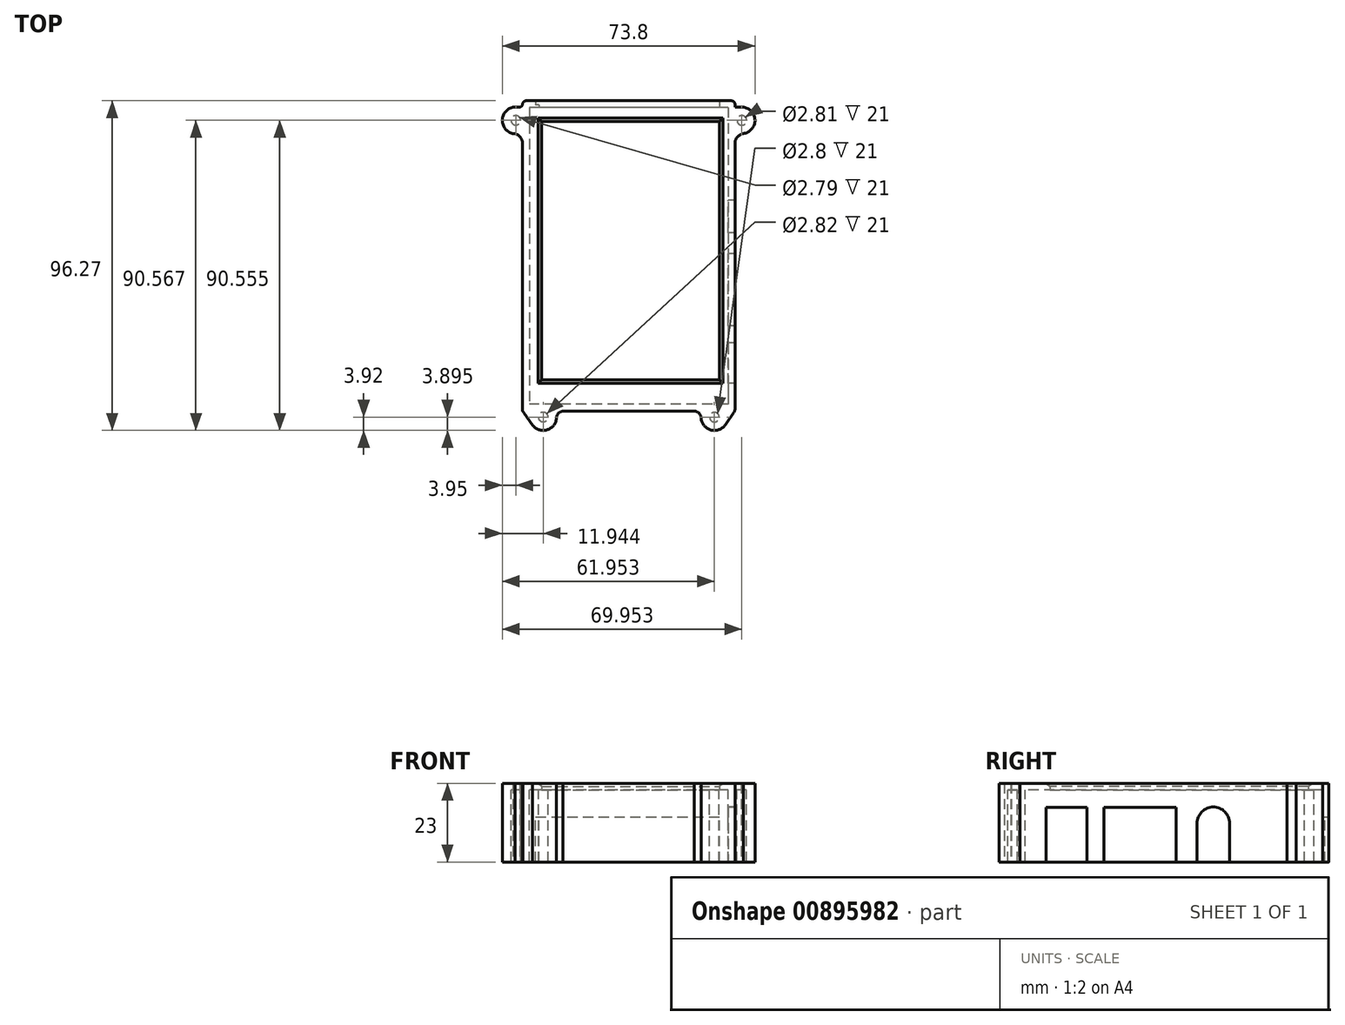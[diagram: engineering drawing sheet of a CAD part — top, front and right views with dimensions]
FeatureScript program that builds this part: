
annotation { "Feature Type Name" : "Feature", "Feature Type Description" : "" }
export const myFeature = defineFeature(function(context is Context, id is Id, definition is map)
    precondition{}
    {
        {
            var Q0;
            Q0=qCreatedBy(makeId("Top.planeOp"),FACE);
            var sketch = newSketch(context, id + "F0", { "sketchPlane" : qUnion([Q0])});
            skLineSegment(sketch, "E0.bottom", {"start": v(21.99, 47.07) * mm, "end": v(-36.05, 47.07) * mm});
            skLineSegment(sketch, "E0.top", {"start": v(21.99, -39.6) * mm, "end": v(-36.05, -39.6) * mm});
            skLineSegment(sketch, "E0.left", {"start": v(21.99, 47.07) * mm, "end": v(21.99, -39.6) * mm});
            skLineSegment(sketch, "E0.right", {"start": v(-36.05, 47.07) * mm, "end": v(-36.05, -39.6) * mm});
            skLineSegment(sketch, "E1.bottom", {"start": v(23.99, 49.03) * mm, "end": v(-38, 49.03) * mm});
            skLineSegment(sketch, "E1.top", {"start": v(23.99, -41.6) * mm, "end": v(-38, -41.6) * mm});
            skLineSegment(sketch, "E1.left", {"start": v(23.99, 49.03) * mm, "end": v(23.99, -41.6) * mm});
            skLineSegment(sketch, "E1.right", {"start": v(-38, 49.03) * mm, "end": v(-38, -41.6) * mm});
            skCircle(sketch, "E2", {"center": v(26, 43.32) * mm, "radius": 1.4 * mm});
            skCircle(sketch, "E3", {"center": v(18, -43.34) * mm, "radius": 1.4 * mm});
            skCircle(sketch, "E4", {"center": v(-32, -43.32) * mm, "radius": 1.41 * mm});
            skCircle(sketch, "E5", {"center": v(-40, 43.33) * mm, "radius": 1.4 * mm});
            skLineSegment(sketch, "E6.bottom", {"start": v(2.04, 49.03) * mm, "end": v(-16.27, 49.03) * mm});
            skLineSegment(sketch, "E6.top", {"start": v(2.04, 47.8) * mm, "end": v(-16.27, 47.8) * mm});
            skLineSegment(sketch, "E6.left", {"start": v(2.04, 49.03) * mm, "end": v(2.04, 47.8) * mm});
            skLineSegment(sketch, "E6.right", {"start": v(-16.27, 49.03) * mm, "end": v(-16.27, 47.8) * mm});
            skLineSegment(sketch, "E7.bottom", {"start": v(-17.75, 49.03) * mm, "end": v(-34.26, 49.03) * mm});
            skLineSegment(sketch, "E7.top", {"start": v(-17.75, 47.8) * mm, "end": v(-34.26, 47.8) * mm});
            skLineSegment(sketch, "E7.left", {"start": v(-17.75, 49.03) * mm, "end": v(-17.75, 47.8) * mm});
            skLineSegment(sketch, "E7.right", {"start": v(-34.26, 49.03) * mm, "end": v(-34.26, 47.8) * mm});
            skLineSegment(sketch, "E8", {"start": v(-33.26, 47.8) * mm, "end": v(-33.26, 47) * mm});
            skLineSegment(sketch, "E9", {"start": v(-15.27, 47.8) * mm, "end": v(-15.27, 45.98) * mm});
            skLineSegment(sketch, "E10", {"start": v(-15.27, 45.98) * mm, "end": v(-18.7, 45.98) * mm});
            skLineSegment(sketch, "E11", {"start": v(-18.7, 45.98) * mm, "end": v(-18.7, 47.8) * mm});
            skLineSegment(sketch, "E12", {"start": v(2.04, 47.8) * mm, "end": v(-0.71, 47.8) * mm});
            skLineSegment(sketch, "E13", {"start": v(-0.71, 47.8) * mm, "end": v(-0.71, 45.98) * mm});
            skLineSegment(sketch, "E14", {"start": v(-0.71, 45.98) * mm, "end": v(2.04, 45.98) * mm});
            skLineSegment(sketch, "E15", {"start": v(2.04, 45.98) * mm, "end": v(2.04, 47.07) * mm});
            skLineSegment(sketch, "E16", {"start": v(2.04, 47.07) * mm, "end": v(2.04, 49.03) * mm});
            skLineSegment(sketch, "E17", {"start": v(2.04, 49.03) * mm, "end": v(2.04, 49.03) * mm});
            skLineSegment(sketch, "E18", {"start": v(19.42, 49.03) * mm, "end": v(19.42, 47.07) * mm});
            skArc(sketch, "E19", {"start": v(26.4, 39.47) * mm, "mid": v(29.84, 43.42) * mm, "end": v(26.2, 47.18) * mm});
            skArc(sketch, "E20", {"start": v(26.2, 47.18) * mm, "mid": v(26, 47.19) * mm, "end": v(25.8, 47.18) * mm});
            skLineSegment(sketch, "E21", {"start": v(25.8, 47.18) * mm, "end": v(23.99, 47.18) * mm});
            skArc(sketch, "E22", {"start": v(26.4, 39.47) * mm, "mid": v(24.75, 38.5) * mm, "end": v(23.99, 36.76) * mm});
            skLineSegment(sketch, "E23.bottom", {"start": v(23.99, 21.28) * mm, "end": v(22.99, 21.28) * mm});
            skLineSegment(sketch, "E23.top", {"start": v(23.99, 11.78) * mm, "end": v(22.99, 11.78) * mm});
            skLineSegment(sketch, "E23.left", {"start": v(23.99, 21.28) * mm, "end": v(23.99, 11.78) * mm});
            skLineSegment(sketch, "E23.right", {"start": v(22.99, 21.28) * mm, "end": v(22.99, 11.78) * mm});
            skLineSegment(sketch, "E24.bottom", {"start": v(22.99, 13) * mm, "end": v(21.99, 13) * mm});
            skLineSegment(sketch, "E24.top", {"start": v(22.99, 20.04) * mm, "end": v(21.99, 20.04) * mm});
            skLineSegment(sketch, "E24.left", {"start": v(22.99, 13) * mm, "end": v(22.99, 20.04) * mm});
            skLineSegment(sketch, "E24.right", {"start": v(21.99, 13) * mm, "end": v(21.99, 20.04) * mm});
            skLineSegment(sketch, "E25", {"start": v(23.99, 5.53) * mm, "end": v(22.99, 5.53) * mm});
            skLineSegment(sketch, "E26", {"start": v(22.99, 5.53) * mm, "end": v(22.5, 5.04) * mm});
            skLineSegment(sketch, "E27", {"start": v(22.5, 5.04) * mm, "end": v(22.5, -15.01) * mm});
            skLineSegment(sketch, "E28", {"start": v(22.5, -15.01) * mm, "end": v(22.99, -15.47) * mm});
            skLineSegment(sketch, "E29", {"start": v(22.99, -15.47) * mm, "end": v(23.99, -15.47) * mm});
            skLineSegment(sketch, "E30", {"start": v(22.99, 5.53) * mm, "end": v(22.99, -15.47) * mm});
            skLineSegment(sketch, "E31", {"start": v(21.99, 7) * mm, "end": v(21.5, 6.56) * mm});
            skLineSegment(sketch, "E32", {"start": v(21.5, 6.56) * mm, "end": v(21.5, 3.27) * mm});
            skLineSegment(sketch, "E33", {"start": v(21.5, 3.27) * mm, "end": v(22.5, 3.27) * mm});
            skLineSegment(sketch, "E34", {"start": v(21.5, 3.27) * mm, "end": v(21.5, -13.23) * mm});
            skLineSegment(sketch, "E35", {"start": v(21.5, -13.23) * mm, "end": v(22.5, -13.23) * mm});
            skLineSegment(sketch, "E36", {"start": v(21.5, -13.23) * mm, "end": v(21.5, -16.5) * mm});
            skLineSegment(sketch, "E37", {"start": v(21.5, -16.5) * mm, "end": v(21.99, -16.96) * mm});
            skLineSegment(sketch, "E38", {"start": v(21.99, -16.96) * mm, "end": v(21.99, -18.86) * mm});
            skLineSegment(sketch, "E39", {"start": v(21.99, -18.86) * mm, "end": v(21.5, -19.34) * mm});
            skLineSegment(sketch, "E40", {"start": v(21.5, -19.34) * mm, "end": v(21.5, -33.42) * mm});
            skLineSegment(sketch, "E41", {"start": v(21.5, -33.42) * mm, "end": v(22.62, -34.44) * mm});
            skLineSegment(sketch, "E42", {"start": v(21.5, -21.89) * mm, "end": v(22.5, -21.85) * mm});
            skLineSegment(sketch, "E43", {"start": v(21.5, -30.87) * mm, "end": v(22.5, -30.87) * mm});
            skLineSegment(sketch, "E44", {"start": v(23.99, -20.4) * mm, "end": v(23.01, -20.4) * mm});
            skLineSegment(sketch, "E45", {"start": v(23.01, -20.4) * mm, "end": v(23.01, -32.4) * mm});
            skLineSegment(sketch, "E46", {"start": v(23.01, -32.4) * mm, "end": v(23.99, -32.4) * mm});
            skLineSegment(sketch, "E47", {"start": v(23.01, -20.4) * mm, "end": v(22.5, -20.86) * mm});
            skLineSegment(sketch, "E48", {"start": v(22.5, -20.86) * mm, "end": v(22.5, -31.86) * mm});
            skLineSegment(sketch, "E49", {"start": v(22.5, -31.86) * mm, "end": v(23.01, -32.4) * mm});
            skLineSegment(sketch, "E50", {"start": v(9.84, -39.6) * mm, "end": v(-0.16, -39.6) * mm});
            skLineSegment(sketch, "E51", {"start": v(-0.16, -39.6) * mm, "end": v(-0.16, -40.6) * mm});
            skLineSegment(sketch, "E52", {"start": v(-0.16, -40.6) * mm, "end": v(1.35, -40.6) * mm});
            skLineSegment(sketch, "E53", {"start": v(1.35, -40.6) * mm, "end": v(1.35, -41.6) * mm});
            skLineSegment(sketch, "E54", {"start": v(9.84, -39.6) * mm, "end": v(9.84, -41.6) * mm});
            skLineSegment(sketch, "E55", {"start": v(-23.65, -39.6) * mm, "end": v(-23.65, -41.6) * mm});
            skLineSegment(sketch, "E56", {"start": v(-13.67, -39.6) * mm, "end": v(-13.67, -40.58) * mm});
            skLineSegment(sketch, "E57", {"start": v(-13.67, -40.58) * mm, "end": v(-15.15, -40.58) * mm});
            skLineSegment(sketch, "E58", {"start": v(-15.15, -40.58) * mm, "end": v(-15.15, -41.6) * mm});
            skLineSegment(sketch, "E59", {"start": v(-0.66, -39.1) * mm, "end": v(-13.16, -39.1) * mm});
            skArc(sketch, "E60", {"start": v(-0.16, -39.6) * mm, "mid": v(-0.3, -39.24) * mm, "end": v(-0.66, -39.1) * mm});
            skArc(sketch, "E61", {"start": v(-13.16, -39.1) * mm, "mid": v(-13.51, -39.24) * mm, "end": v(-13.66, -39.6) * mm});
            skArc(sketch, "E62", {"start": v(-35.1, -45.7) * mm, "mid": v(-30.94, -47.08) * mm, "end": v(-28.12, -43.72) * mm});
            skArc(sketch, "E63", {"start": v(-26.26, -41.6) * mm, "mid": v(-27.63, -42.28) * mm, "end": v(-28.12, -43.72) * mm});
            skLineSegment(sketch, "E64", {"start": v(-35.1, -45.7) * mm, "end": v(-37.6, -42.18) * mm});
            skArc(sketch, "E65", {"start": v(-40.81, 47.19) * mm, "mid": v(-43.93, 43.02) * mm, "end": v(-40.2, 39.39) * mm});
            skArc(sketch, "E66", {"start": v(-38, 36.69) * mm, "mid": v(-38.68, 38.39) * mm, "end": v(-40.2, 39.39) * mm});
            skArc(sketch, "E67", {"start": v(-38.87, 47.19) * mm, "mid": v(-38.28, 47.5) * mm, "end": v(-38, 48.1) * mm});
            skLineSegment(sketch, "E68", {"start": v(-38.87, 47.19) * mm, "end": v(-40.81, 47.19) * mm});
            skArc(sketch, "E69", {"start": v(14.14, -43.87) * mm, "mid": v(17.09, -47.13) * mm, "end": v(21.2, -45.57) * mm});
            skArc(sketch, "E70", {"start": v(23.68, -42.01) * mm, "mid": v(23.89, -41.6) * mm, "end": v(23.99, -41.15) * mm});
            skLineSegment(sketch, "E71", {"start": v(23.68, -42.01) * mm, "end": v(21.2, -45.57) * mm});
            skArc(sketch, "E72", {"start": v(14.09, -43.4) * mm, "mid": v(13.46, -42.14) * mm, "end": v(12.16, -41.6) * mm});
            skLineSegment(sketch, "E73", {"start": v(14.09, -43.4) * mm, "end": v(14.14, -43.87) * mm});
            skPoint(sketch, "E74", {"position": v(-37.9, -41.6) * mm});
            skArc(sketch, "E75", {"start": v(-37.9, -41.6) * mm, "mid": v(-37.77, -41.9) * mm, "end": v(-37.6, -42.18) * mm});
            skArc(sketch, "E76", {"start": v(-38, -41.1) * mm, "mid": v(-37.98, -41.36) * mm, "end": v(-37.9, -41.6) * mm});
            skLineSegment(sketch, "E77", {"start": v(21.55, 21.53) * mm, "end": v(23.99, 21.53) * mm, "construction": true});
            skLineSegment(sketch, "E78.bottom", {"start": v(-32.5, -32.47) * mm, "end": v(19.5, -32.47) * mm});
            skLineSegment(sketch, "E78.top", {"start": v(-32.5, 43.03) * mm, "end": v(19.5, 43.03) * mm});
            skLineSegment(sketch, "E78.left", {"start": v(-32.5, -32.47) * mm, "end": v(-32.5, 43.03) * mm});
            skLineSegment(sketch, "E78.right", {"start": v(19.5, -32.47) * mm, "end": v(19.5, 43.03) * mm});
            skSolve(sketch);
        }
        {
            var Q0;
            {var subQ3=sQuery(id+"F0.wireOp",EDGE,"E6.left");Q0=makeQuery(id+"F0.imprint","IMPRINT",FACE,{"disambiguationData":[TD([[makeQuery(id+"F0.imprint","IMPRINT",EDGE,{"derivedFrom":subQ3}),1.0]])]});}
            var Q1;
            {var subQ0=sQuery(id+"F0.wireOp",EDGE,"E18");Q1=makeQuery(id+"F0.imprint","IMPRINT",FACE,{"disambiguationData":[TD([[makeQuery(id+"F0.imprint","IMPRINT",EDGE,{"derivedFrom":subQ0}),1.0]])]});}
            var Q2;
            Q2=makeQuery(id+"F0.imprint","IMPRINT",FACE,{"disambiguationData":[TD([[makeQuery(id+"F0.imprint","IMPRINT",EDGE,{"derivedFrom":sQuery(id+"F0.wireOp",EDGE,"E2")}),-1.0]])]});
            var Q3;
            {var subQ0=sQuery(id+"F0.wireOp",EDGE,"E24.bottom");Q3=makeQuery(id+"F0.imprint","IMPRINT",FACE,{"disambiguationData":[TD([[makeQuery(id+"F0.imprint","IMPRINT",EDGE,{"derivedFrom":subQ0}),-1.0]])]});}
            var Q4;
            {var subQ3=sQuery(id+"F0.wireOp",EDGE,"E23.bottom");Q4=makeQuery(id+"F0.imprint","IMPRINT",FACE,{"disambiguationData":[TD([[makeQuery(id+"F0.imprint","IMPRINT",EDGE,{"derivedFrom":subQ3}),1.0]])]});}
            var Q5;
            {var subQ2=sQuery(id+"F0.wireOp",EDGE,"E23.top");Q5=makeQuery(id+"F0.imprint","IMPRINT",FACE,{"disambiguationData":[TD([[makeQuery(id+"F0.imprint","IMPRINT",EDGE,{"derivedFrom":subQ2}),1.0]])]});}
            var Q6;
            {var subQ0=sQuery(id+"F0.wireOp",EDGE,"E33");var subQ1=sQuery(id+"F0.wireOp",EDGE,"E0.left");var subQ2=makeQuery(id+"F0.imprint","INTERSECT",VERTEX,{"derivedFrom":[subQ1,subQ0]});Q6=makeQuery(id+"F0.imprint","IMPRINT",FACE,{"disambiguationData":[TD([[makeQuery(id+"F0.imprint","IMPRINT",EDGE,{"disambiguationData":[TD([[subQ2,-1.0]])],"derivedFrom":subQ1}),1.0]])]});}
            var Q7;
            {var subQ0=sQuery(id+"F0.wireOp",EDGE,"E25");Q7=makeQuery(id+"F0.imprint","IMPRINT",FACE,{"disambiguationData":[TD([[makeQuery(id+"F0.imprint","IMPRINT",EDGE,{"derivedFrom":subQ0}),1.0]])]});}
            var Q8;
            {var subQ1=sQuery(id+"F0.wireOp",EDGE,"E26");Q8=makeQuery(id+"F0.imprint","IMPRINT",FACE,{"disambiguationData":[TD([[makeQuery(id+"F0.imprint","IMPRINT",EDGE,{"derivedFrom":subQ1}),1.0]])]});}
            var Q9;
            {var subQ21=sQuery(id+"F0.wireOp",EDGE,"E0.right");Q9=makeQuery(id+"F0.imprint","IMPRINT",FACE,{"disambiguationData":[TD([[makeQuery(id+"F0.imprint","IMPRINT",EDGE,{"derivedFrom":subQ21}),1.0]])]});}
            var Q10;
            {var subQ1=sQuery(id+"F0.wireOp",EDGE,"E28");Q10=makeQuery(id+"F0.imprint","IMPRINT",FACE,{"disambiguationData":[TD([[makeQuery(id+"F0.imprint","IMPRINT",EDGE,{"derivedFrom":subQ1}),-1.0]])]});}
            var Q11;
            {var subQ4=sQuery(id+"F0.wireOp",EDGE,"E36");Q11=makeQuery(id+"F0.imprint","IMPRINT",FACE,{"disambiguationData":[TD([[makeQuery(id+"F0.imprint","IMPRINT",EDGE,{"derivedFrom":subQ4}),1.0]])]});}
            var Q12;
            {var subQ0=sQuery(id+"F0.wireOp",EDGE,"E39");Q12=makeQuery(id+"F0.imprint","IMPRINT",FACE,{"disambiguationData":[TD([[makeQuery(id+"F0.imprint","IMPRINT",EDGE,{"derivedFrom":subQ0}),1.0]])]});}
            var Q13;
            {var subQ0=sQuery(id+"F0.wireOp",EDGE,"E42");var subQ1=sQuery(id+"F0.wireOp",EDGE,"E0.left");var subQ2=makeQuery(id+"F0.imprint","INTERSECT",VERTEX,{"derivedFrom":[subQ1,subQ0]});Q13=makeQuery(id+"F0.imprint","IMPRINT",FACE,{"disambiguationData":[TD([[makeQuery(id+"F0.imprint","IMPRINT",EDGE,{"disambiguationData":[TD([[subQ2,-1.0]])],"derivedFrom":subQ1}),-1.0]])]});}
            var Q14;
            {var subQ0=sQuery(id+"F0.wireOp",EDGE,"E42");var subQ1=sQuery(id+"F0.wireOp",EDGE,"E0.left");var subQ2=makeQuery(id+"F0.imprint","INTERSECT",VERTEX,{"derivedFrom":[subQ1,subQ0]});Q14=makeQuery(id+"F0.imprint","IMPRINT",FACE,{"disambiguationData":[TD([[makeQuery(id+"F0.imprint","IMPRINT",EDGE,{"disambiguationData":[TD([[subQ2,-1.0]])],"derivedFrom":subQ1}),1.0]])]});}
            var Q15;
            Q15=makeQuery(id+"F0.imprint","IMPRINT",FACE,{"disambiguationData":[TD([[makeQuery(id+"F0.imprint","IMPRINT",EDGE,{"derivedFrom":sQuery(id+"F0.wireOp",EDGE,"E45")}),-1.0]])]});
            var Q16;
            {var subQ0=sQuery(id+"F0.wireOp",EDGE,"E44");Q16=makeQuery(id+"F0.imprint","IMPRINT",FACE,{"disambiguationData":[TD([[makeQuery(id+"F0.imprint","IMPRINT",EDGE,{"derivedFrom":subQ0}),1.0]])]});}
            var Q17;
            {var subQ5=sQuery(id+"F0.wireOp",EDGE,"E34");Q17=makeQuery(id+"F0.imprint","IMPRINT",FACE,{"disambiguationData":[TD([[makeQuery(id+"F0.imprint","IMPRINT",EDGE,{"derivedFrom":subQ5}),1.0]])]});}
            var Q18;
            {var subQ0=sQuery(id+"F0.wireOp",EDGE,"E31");Q18=makeQuery(id+"F0.imprint","IMPRINT",FACE,{"disambiguationData":[TD([[makeQuery(id+"F0.imprint","IMPRINT",EDGE,{"derivedFrom":subQ0}),1.0]])]});}
            var Q19;
            {var subQ0=sQuery(id+"F0.wireOp",EDGE,"E41");var subQ1=sQuery(id+"F0.wireOp",EDGE,"E0.left");var subQ2=makeQuery(id+"F0.imprint","INTERSECT",VERTEX,{"derivedFrom":[subQ1,subQ0]});Q19=makeQuery(id+"F0.imprint","IMPRINT",FACE,{"disambiguationData":[TD([[makeQuery(id+"F0.imprint","IMPRINT",EDGE,{"disambiguationData":[TD([[subQ2,1.0]])],"derivedFrom":subQ1}),-1.0]])]});}
            var Q20;
            {var subQ1=sQuery(id+"F0.wireOp",EDGE,"E46");Q20=makeQuery(id+"F0.imprint","IMPRINT",FACE,{"disambiguationData":[TD([[makeQuery(id+"F0.imprint","IMPRINT",EDGE,{"derivedFrom":subQ1}),-1.0]])]});}
            var Q21;
            Q21=makeQuery(id+"F0.imprint","IMPRINT",FACE,{"disambiguationData":[TD([[makeQuery(id+"F0.imprint","IMPRINT",EDGE,{"derivedFrom":sQuery(id+"F0.wireOp",EDGE,"E3")}),-1.0]])]});
            var Q22;
            {var subQ1=sQuery(id+"F0.wireOp",EDGE,"E55");Q22=makeQuery(id+"F0.imprint","IMPRINT",FACE,{"disambiguationData":[TD([[makeQuery(id+"F0.imprint","IMPRINT",EDGE,{"derivedFrom":subQ1}),1.0]])]});}
            var Q23;
            {var subQ4=sQuery(id+"F0.wireOp",EDGE,"E0.right");Q23=makeQuery(id+"F0.imprint","IMPRINT",FACE,{"disambiguationData":[TD([[makeQuery(id+"F0.imprint","IMPRINT",EDGE,{"derivedFrom":subQ4}),-1.0]])]});}
            var Q24;
            {var subQ0=sQuery(id+"F0.wireOp",EDGE,"E51");Q24=makeQuery(id+"F0.imprint","IMPRINT",FACE,{"disambiguationData":[TD([[makeQuery(id+"F0.imprint","IMPRINT",EDGE,{"derivedFrom":subQ0}),-1.0]])]});}
            var Q25;
            {var subQ0=sQuery(id+"F0.wireOp",EDGE,"E51");Q25=makeQuery(id+"F0.imprint","IMPRINT",FACE,{"disambiguationData":[TD([[makeQuery(id+"F0.imprint","IMPRINT",EDGE,{"derivedFrom":subQ0}),1.0]])]});}
            var Q26;
            Q26=makeQuery(id+"F0.imprint","IMPRINT",FACE,{"disambiguationData":[TD([[makeQuery(id+"F0.imprint","IMPRINT",EDGE,{"derivedFrom":sQuery(id+"F0.wireOp",EDGE,"E59")}),1.0]])]});
            var Q27;
            Q27=makeQuery(id+"F0.imprint","IMPRINT",FACE,{"disambiguationData":[TD([[makeQuery(id+"F0.imprint","IMPRINT",EDGE,{"derivedFrom":sQuery(id+"F0.wireOp",EDGE,"E4")}),-1.0]])]});
            var Q28;
            Q28=makeQuery(id+"F0.imprint","IMPRINT",FACE,{"disambiguationData":[TD([[makeQuery(id+"F0.imprint","IMPRINT",EDGE,{"derivedFrom":sQuery(id+"F0.wireOp",EDGE,"E5")}),-1.0]])]});
            var Q29;
            {var subQ0=sQuery(id+"F0.wireOp",EDGE,"E8");var subQ1=sQuery(id+"F0.wireOp",EDGE,"E0.bottom");var subQ2=makeQuery(id+"F0.imprint","INTERSECT",VERTEX,{"derivedFrom":[subQ1,subQ0]});Q29=makeQuery(id+"F0.imprint","IMPRINT",FACE,{"disambiguationData":[TD([[makeQuery(id+"F0.imprint","IMPRINT",EDGE,{"disambiguationData":[TD([[subQ2,1.0]])],"derivedFrom":subQ1}),-1.0]])]});}
            var Q30;
            {var subQ2=sQuery(id+"F0.wireOp",EDGE,"E7.left");Q30=makeQuery(id+"F0.imprint","IMPRINT",FACE,{"disambiguationData":[TD([[makeQuery(id+"F0.imprint","IMPRINT",EDGE,{"derivedFrom":subQ2}),-1.0]])]});}
            var Q31;
            {var subQ5=sQuery(id+"F0.wireOp",EDGE,"E10");Q31=makeQuery(id+"F0.imprint","IMPRINT",FACE,{"disambiguationData":[TD([[makeQuery(id+"F0.imprint","IMPRINT",EDGE,{"derivedFrom":subQ5}),-1.0]])]});}
            var Q32;
            {var subQ0=sQuery(id+"F0.wireOp",EDGE,"E6.right");Q32=makeQuery(id+"F0.imprint","IMPRINT",FACE,{"disambiguationData":[TD([[makeQuery(id+"F0.imprint","IMPRINT",EDGE,{"derivedFrom":subQ0}),-1.0]])]});}
            var Q33;
            {var subQ0=sQuery(id+"F0.wireOp",EDGE,"E9");var subQ1=sQuery(id+"F0.wireOp",EDGE,"E0.bottom");var subQ2=makeQuery(id+"F0.imprint","INTERSECT",VERTEX,{"derivedFrom":[subQ1,subQ0]});Q33=makeQuery(id+"F0.imprint","IMPRINT",FACE,{"disambiguationData":[TD([[makeQuery(id+"F0.imprint","IMPRINT",EDGE,{"disambiguationData":[TD([[subQ2,1.0]])],"derivedFrom":subQ1}),-1.0]])]});}
            var Q34;
            {var subQ4=sQuery(id+"F0.wireOp",EDGE,"E6.left");Q34=makeQuery(id+"F0.imprint","IMPRINT",FACE,{"disambiguationData":[TD([[makeQuery(id+"F0.imprint","IMPRINT",EDGE,{"derivedFrom":subQ4}),-1.0]])]});}
            var Q35;
            {var subQ4=sQuery(id+"F0.wireOp",EDGE,"E14");Q35=makeQuery(id+"F0.imprint","IMPRINT",FACE,{"disambiguationData":[TD([[makeQuery(id+"F0.imprint","IMPRINT",EDGE,{"derivedFrom":subQ4}),1.0]])]});}
            var Q36;
            {var subQ3=sQuery(id+"F0.wireOp",EDGE,"E16");Q36=makeQuery(id+"F0.imprint","IMPRINT",FACE,{"disambiguationData":[TD([[makeQuery(id+"F0.imprint","IMPRINT",EDGE,{"derivedFrom":subQ3}),1.0]])]});}
            var Q37;
            Q37=makeQuery(id+"F0.imprint","IMPRINT",FACE,{"disambiguationData":[TD([[makeQuery(id+"F0.imprint","IMPRINT",EDGE,{"derivedFrom":sQuery(id+"F0.wireOp",EDGE,"E4")}),1.0]])]});
            var Q38;
            Q38=makeQuery(id+"F0.imprint","IMPRINT",FACE,{"disambiguationData":[TD([[makeQuery(id+"F0.imprint","IMPRINT",EDGE,{"derivedFrom":sQuery(id+"F0.wireOp",EDGE,"E5")}),1.0]])]});
            var Q39;
            Q39=makeQuery(id+"F0.imprint","IMPRINT",FACE,{"disambiguationData":[TD([[makeQuery(id+"F0.imprint","IMPRINT",EDGE,{"derivedFrom":sQuery(id+"F0.wireOp",EDGE,"E2")}),1.0]])]});
            var Q40;
            Q40=makeQuery(id+"F0.imprint","IMPRINT",FACE,{"disambiguationData":[TD([[makeQuery(id+"F0.imprint","IMPRINT",EDGE,{"derivedFrom":sQuery(id+"F0.wireOp",EDGE,"E3")}),1.0]])]});
            extrude(context, id + "F1", {"entities" : qUnion([Q0, Q1, Q2, Q3, Q4, Q5, Q6, Q7, Q8, Q9, Q10, Q11, Q12, Q13, Q14, Q15, Q16, Q17, Q18, Q19, Q20, Q21, Q22, Q23, Q24, Q25, Q26, Q27, Q28, Q29, Q30, Q31, Q32, Q33, Q34, Q35, Q36, Q37, Q38, Q39, Q40]), "depth" : 2 * mm, "offsetDistance" : 25 * mm});
        }
        {
            var Q0;
            {var subQ4=sQuery(id+"F0.wireOp",EDGE,"E0.right");Q0=makeQuery(id+"F0.imprint","IMPRINT",FACE,{"disambiguationData":[TD([[makeQuery(id+"F0.imprint","IMPRINT",EDGE,{"derivedFrom":subQ4}),-1.0]])]});}
            var Q1;
            {var subQ1=sQuery(id+"F0.wireOp",EDGE,"E55");Q1=makeQuery(id+"F0.imprint","IMPRINT",FACE,{"disambiguationData":[TD([[makeQuery(id+"F0.imprint","IMPRINT",EDGE,{"derivedFrom":subQ1}),1.0]])]});}
            var Q2;
            Q2=makeQuery(id+"F0.imprint","IMPRINT",FACE,{"disambiguationData":[TD([[makeQuery(id+"F0.imprint","IMPRINT",EDGE,{"derivedFrom":sQuery(id+"F0.wireOp",EDGE,"E4")}),-1.0]])]});
            var Q3;
            Q3=makeQuery(id+"F0.imprint","IMPRINT",FACE,{"disambiguationData":[TD([[makeQuery(id+"F0.imprint","IMPRINT",EDGE,{"derivedFrom":sQuery(id+"F0.wireOp",EDGE,"E3")}),-1.0]])]});
            var Q4;
            {var subQ1=sQuery(id+"F0.wireOp",EDGE,"E46");Q4=makeQuery(id+"F0.imprint","IMPRINT",FACE,{"disambiguationData":[TD([[makeQuery(id+"F0.imprint","IMPRINT",EDGE,{"derivedFrom":subQ1}),-1.0]])]});}
            var Q5;
            {var subQ0=sQuery(id+"F0.wireOp",EDGE,"E51");Q5=makeQuery(id+"F0.imprint","IMPRINT",FACE,{"disambiguationData":[TD([[makeQuery(id+"F0.imprint","IMPRINT",EDGE,{"derivedFrom":subQ0}),1.0]])]});}
            var Q6;
            {var subQ0=sQuery(id+"F0.wireOp",EDGE,"E51");Q6=makeQuery(id+"F0.imprint","IMPRINT",FACE,{"disambiguationData":[TD([[makeQuery(id+"F0.imprint","IMPRINT",EDGE,{"derivedFrom":subQ0}),-1.0]])]});}
            var Q7;
            {var subQ0=sQuery(id+"F0.wireOp",EDGE,"E44");Q7=makeQuery(id+"F0.imprint","IMPRINT",FACE,{"disambiguationData":[TD([[makeQuery(id+"F0.imprint","IMPRINT",EDGE,{"derivedFrom":subQ0}),1.0]])]});}
            var Q8;
            {var subQ1=sQuery(id+"F0.wireOp",EDGE,"E28");Q8=makeQuery(id+"F0.imprint","IMPRINT",FACE,{"disambiguationData":[TD([[makeQuery(id+"F0.imprint","IMPRINT",EDGE,{"derivedFrom":subQ1}),-1.0]])]});}
            var Q9;
            {var subQ0=sQuery(id+"F0.wireOp",EDGE,"E25");Q9=makeQuery(id+"F0.imprint","IMPRINT",FACE,{"disambiguationData":[TD([[makeQuery(id+"F0.imprint","IMPRINT",EDGE,{"derivedFrom":subQ0}),1.0]])]});}
            var Q10;
            {var subQ2=sQuery(id+"F0.wireOp",EDGE,"E23.top");Q10=makeQuery(id+"F0.imprint","IMPRINT",FACE,{"disambiguationData":[TD([[makeQuery(id+"F0.imprint","IMPRINT",EDGE,{"derivedFrom":subQ2}),1.0]])]});}
            var Q11;
            {var subQ3=sQuery(id+"F0.wireOp",EDGE,"E23.bottom");Q11=makeQuery(id+"F0.imprint","IMPRINT",FACE,{"disambiguationData":[TD([[makeQuery(id+"F0.imprint","IMPRINT",EDGE,{"derivedFrom":subQ3}),1.0]])]});}
            var Q12;
            {var subQ0=sQuery(id+"F0.wireOp",EDGE,"E24.bottom");Q12=makeQuery(id+"F0.imprint","IMPRINT",FACE,{"disambiguationData":[TD([[makeQuery(id+"F0.imprint","IMPRINT",EDGE,{"derivedFrom":subQ0}),-1.0]])]});}
            var Q13;
            {var subQ0=sQuery(id+"F0.wireOp",EDGE,"E18");Q13=makeQuery(id+"F0.imprint","IMPRINT",FACE,{"disambiguationData":[TD([[makeQuery(id+"F0.imprint","IMPRINT",EDGE,{"derivedFrom":subQ0}),1.0]])]});}
            var Q14;
            Q14=makeQuery(id+"F0.imprint","IMPRINT",FACE,{"disambiguationData":[TD([[makeQuery(id+"F0.imprint","IMPRINT",EDGE,{"derivedFrom":sQuery(id+"F0.wireOp",EDGE,"E2")}),-1.0]])]});
            var Q15;
            {var subQ3=sQuery(id+"F0.wireOp",EDGE,"E6.left");Q15=makeQuery(id+"F0.imprint","IMPRINT",FACE,{"disambiguationData":[TD([[makeQuery(id+"F0.imprint","IMPRINT",EDGE,{"derivedFrom":subQ3}),1.0]])]});}
            var Q16;
            {var subQ4=sQuery(id+"F0.wireOp",EDGE,"E6.left");Q16=makeQuery(id+"F0.imprint","IMPRINT",FACE,{"disambiguationData":[TD([[makeQuery(id+"F0.imprint","IMPRINT",EDGE,{"derivedFrom":subQ4}),-1.0]])]});}
            var Q17;
            {var subQ2=sQuery(id+"F0.wireOp",EDGE,"E7.left");Q17=makeQuery(id+"F0.imprint","IMPRINT",FACE,{"disambiguationData":[TD([[makeQuery(id+"F0.imprint","IMPRINT",EDGE,{"derivedFrom":subQ2}),-1.0]])]});}
            var Q18;
            Q18=makeQuery(id+"F0.imprint","IMPRINT",FACE,{"disambiguationData":[TD([[makeQuery(id+"F0.imprint","IMPRINT",EDGE,{"derivedFrom":sQuery(id+"F0.wireOp",EDGE,"E5")}),-1.0]])]});
            var Q19;
            {var subQ0=sQuery(id+"F0.wireOp",EDGE,"E9");var subQ1=sQuery(id+"F0.wireOp",EDGE,"E0.bottom");var subQ2=makeQuery(id+"F0.imprint","INTERSECT",VERTEX,{"derivedFrom":[subQ1,subQ0]});Q19=makeQuery(id+"F0.imprint","IMPRINT",FACE,{"disambiguationData":[TD([[makeQuery(id+"F0.imprint","IMPRINT",EDGE,{"disambiguationData":[TD([[subQ2,1.0]])],"derivedFrom":subQ1}),-1.0]])]});}
            var Q20;
            {var subQ0=sQuery(id+"F0.wireOp",EDGE,"E8");var subQ1=sQuery(id+"F0.wireOp",EDGE,"E0.bottom");var subQ2=makeQuery(id+"F0.imprint","INTERSECT",VERTEX,{"derivedFrom":[subQ1,subQ0]});Q20=makeQuery(id+"F0.imprint","IMPRINT",FACE,{"disambiguationData":[TD([[makeQuery(id+"F0.imprint","IMPRINT",EDGE,{"disambiguationData":[TD([[subQ2,1.0]])],"derivedFrom":subQ1}),-1.0]])]});}
            var Q21;
            {var subQ0=sQuery(id+"F0.wireOp",EDGE,"E42");var subQ1=sQuery(id+"F0.wireOp",EDGE,"E0.left");var subQ2=makeQuery(id+"F0.imprint","INTERSECT",VERTEX,{"derivedFrom":[subQ1,subQ0]});Q21=makeQuery(id+"F0.imprint","IMPRINT",FACE,{"disambiguationData":[TD([[makeQuery(id+"F0.imprint","IMPRINT",EDGE,{"disambiguationData":[TD([[subQ2,-1.0]])],"derivedFrom":subQ1}),1.0]])]});}
            var Q22;
            Q22=makeQuery(id+"F0.imprint","IMPRINT",FACE,{"disambiguationData":[TD([[makeQuery(id+"F0.imprint","IMPRINT",EDGE,{"derivedFrom":sQuery(id+"F0.wireOp",EDGE,"E45")}),-1.0]])]});
            var Q23;
            {var subQ1=sQuery(id+"F0.wireOp",EDGE,"E26");Q23=makeQuery(id+"F0.imprint","IMPRINT",FACE,{"disambiguationData":[TD([[makeQuery(id+"F0.imprint","IMPRINT",EDGE,{"derivedFrom":subQ1}),1.0]])]});}
            var Q24;
            {var subQ0=sQuery(id+"F0.wireOp",EDGE,"E33");var subQ1=sQuery(id+"F0.wireOp",EDGE,"E0.left");var subQ2=makeQuery(id+"F0.imprint","INTERSECT",VERTEX,{"derivedFrom":[subQ1,subQ0]});Q24=makeQuery(id+"F0.imprint","IMPRINT",FACE,{"disambiguationData":[TD([[makeQuery(id+"F0.imprint","IMPRINT",EDGE,{"disambiguationData":[TD([[subQ2,-1.0]])],"derivedFrom":subQ1}),1.0]])]});}
            var Q25;
            {var subQ0=sQuery(id+"F0.wireOp",EDGE,"E6.right");Q25=makeQuery(id+"F0.imprint","IMPRINT",FACE,{"disambiguationData":[TD([[makeQuery(id+"F0.imprint","IMPRINT",EDGE,{"derivedFrom":subQ0}),-1.0]])]});}
            var Q26;
            {var subQ3=sQuery(id+"F0.wireOp",EDGE,"E16");Q26=makeQuery(id+"F0.imprint","IMPRINT",FACE,{"disambiguationData":[TD([[makeQuery(id+"F0.imprint","IMPRINT",EDGE,{"derivedFrom":subQ3}),1.0]])]});}
            extrude(context, id + "F2", {"entities" : qUnion([Q0, Q1, Q2, Q3, Q4, Q5, Q6, Q7, Q8, Q9, Q10, Q11, Q12, Q13, Q14, Q15, Q16, Q17, Q18, Q19, Q20, Q21, Q22, Q23, Q24, Q25, Q26]), "operationType" : NewBodyOperationType.ADD, "oppositeDirection" : true, "depth" : 21 * mm, "offsetDistance" : 25 * mm});
        }
        {
            var Q0;
            {var subQ2=sQuery(id+"F0.wireOp",EDGE,"E7.left");Q0=makeQuery(id+"F0.imprint","IMPRINT",FACE,{"disambiguationData":[TD([[makeQuery(id+"F0.imprint","IMPRINT",EDGE,{"derivedFrom":subQ2}),-1.0]])]});}
            var Q1;
            {var subQ0=sQuery(id+"F0.wireOp",EDGE,"E6.right");Q1=makeQuery(id+"F0.imprint","IMPRINT",FACE,{"disambiguationData":[TD([[makeQuery(id+"F0.imprint","IMPRINT",EDGE,{"derivedFrom":subQ0}),-1.0]])]});}
            var Q2;
            {var subQ4=sQuery(id+"F0.wireOp",EDGE,"E6.left");Q2=makeQuery(id+"F0.imprint","IMPRINT",FACE,{"disambiguationData":[TD([[makeQuery(id+"F0.imprint","IMPRINT",EDGE,{"derivedFrom":subQ4}),-1.0]])]});}
            var Q3;
            {var subQ0=sQuery(id+"F0.wireOp",EDGE,"E8");var subQ1=sQuery(id+"F0.wireOp",EDGE,"E0.bottom");var subQ2=makeQuery(id+"F0.imprint","INTERSECT",VERTEX,{"derivedFrom":[subQ1,subQ0]});Q3=makeQuery(id+"F0.imprint","IMPRINT",FACE,{"disambiguationData":[TD([[makeQuery(id+"F0.imprint","IMPRINT",EDGE,{"disambiguationData":[TD([[subQ2,1.0]])],"derivedFrom":subQ1}),-1.0]])]});}
            var Q4;
            {var subQ0=sQuery(id+"F0.wireOp",EDGE,"E9");var subQ1=sQuery(id+"F0.wireOp",EDGE,"E0.bottom");var subQ2=makeQuery(id+"F0.imprint","INTERSECT",VERTEX,{"derivedFrom":[subQ1,subQ0]});Q4=makeQuery(id+"F0.imprint","IMPRINT",FACE,{"disambiguationData":[TD([[makeQuery(id+"F0.imprint","IMPRINT",EDGE,{"disambiguationData":[TD([[subQ2,1.0]])],"derivedFrom":subQ1}),-1.0]])]});}
            var Q5;
            {var subQ3=sQuery(id+"F0.wireOp",EDGE,"E16");Q5=makeQuery(id+"F0.imprint","IMPRINT",FACE,{"disambiguationData":[TD([[makeQuery(id+"F0.imprint","IMPRINT",EDGE,{"derivedFrom":subQ3}),1.0]])]});}
            var Q6;
            {var subQ3=sQuery(id+"F0.wireOp",EDGE,"E6.left");Q6=makeQuery(id+"F0.imprint","IMPRINT",FACE,{"disambiguationData":[TD([[makeQuery(id+"F0.imprint","IMPRINT",EDGE,{"derivedFrom":subQ3}),1.0]])]});}
            extrude(context, id + "F3", {"entities" : qUnion([Q0, Q1, Q2, Q3, Q4, Q5, Q6]), "operationType" : NewBodyOperationType.REMOVE, "oppositeDirection" : true, "depth" : 25 * mm, "offsetDistance" : 25 * mm, "hasSecondDirection" : true, "secondDirectionOppositeDirection" : true, "secondDirectionDepth" : 8 * mm});
        }
        {
            var Q0;
            Q0=qCreatedBy(makeId("Right.planeOp"),FACE);
            var sketch = newSketch(context, id + "F4", { "sketchPlane" : qUnion([Q0])});
            skCircle(sketch, "E79", {"center": v(15.28, -9.68) * mm, "radius": 4.75 * mm});
            skLineSegment(sketch, "E80.bottom", {"start": v(10.53, 25.1) * mm, "end": v(20.03, 25.1) * mm});
            skLineSegment(sketch, "E80.top", {"start": v(10.53, 3.24) * mm, "end": v(20.03, 3.24) * mm});
            skLineSegment(sketch, "E80.left", {"start": v(10.53, 25.1) * mm, "end": v(10.53, 3.24) * mm});
            skLineSegment(sketch, "E80.right", {"start": v(20.03, 25.1) * mm, "end": v(20.03, 3.24) * mm});
            skLineSegment(sketch, "E81.bottom", {"start": v(-16.66, 29) * mm, "end": v(4.34, 29) * mm});
            skLineSegment(sketch, "E81.top", {"start": v(-16.66, 9.12) * mm, "end": v(4.34, 9.12) * mm});
            skLineSegment(sketch, "E81.left", {"start": v(-16.66, 29) * mm, "end": v(-16.66, 9.12) * mm});
            skLineSegment(sketch, "E81.right", {"start": v(4.34, 29) * mm, "end": v(4.34, 9.12) * mm});
            skLineSegment(sketch, "E82.bottom", {"start": v(-33.52, 29) * mm, "end": v(-21.65, 29) * mm});
            skLineSegment(sketch, "E82.top", {"start": v(-33.52, 8.94) * mm, "end": v(-21.65, 8.94) * mm});
            skLineSegment(sketch, "E82.left", {"start": v(-33.52, 29) * mm, "end": v(-33.52, 8.94) * mm});
            skLineSegment(sketch, "E82.right", {"start": v(-21.65, 29) * mm, "end": v(-21.65, 8.94) * mm});
            skLineSegment(sketch, "E83", {"start": v(-53.53, -5) * mm, "end": v(59.97, -5) * mm, "construction": true});
            skLineSegment(sketch, "E84.bottom", {"start": v(-16.66, -5) * mm, "end": v(4.34, -5) * mm});
            skLineSegment(sketch, "E84.top", {"start": v(-16.66, -28.7) * mm, "end": v(4.34, -28.7) * mm});
            skLineSegment(sketch, "E84.left", {"start": v(-16.66, -5) * mm, "end": v(-16.66, -28.7) * mm});
            skLineSegment(sketch, "E84.right", {"start": v(4.34, -5) * mm, "end": v(4.34, -28.7) * mm});
            skLineSegment(sketch, "E85.bottom", {"start": v(-33.52, -5) * mm, "end": v(-21.65, -5) * mm});
            skLineSegment(sketch, "E85.top", {"start": v(-33.52, -28.7) * mm, "end": v(-21.65, -28.7) * mm});
            skLineSegment(sketch, "E85.left", {"start": v(-33.52, -5) * mm, "end": v(-33.52, -28.7) * mm});
            skLineSegment(sketch, "E85.right", {"start": v(-21.65, -5) * mm, "end": v(-21.65, -28.7) * mm});
            skLineSegment(sketch, "E86.bottom", {"start": v(10.53, -9.68) * mm, "end": v(20.03, -9.68) * mm});
            skLineSegment(sketch, "E86.top", {"start": v(10.53, -25.3) * mm, "end": v(20.03, -25.3) * mm});
            skLineSegment(sketch, "E86.left", {"start": v(10.53, -9.68) * mm, "end": v(10.53, -25.3) * mm});
            skLineSegment(sketch, "E86.right", {"start": v(20.03, -9.68) * mm, "end": v(20.03, -25.3) * mm});
            skSolve(sketch);
        }
        {
            var Q0;
            {var subQ0=sQuery(id+"F4.wireOp",EDGE,"E86.bottom");var subQ1=sQuery(id+"F4.wireOp",EDGE,"E79");var subQ3=makeQuery(id+"F4.imprint","INTERSECT",VERTEX,{"derivedFrom":[subQ1,subQ0]});Q0=makeQuery(id+"F4.imprint","IMPRINT",FACE,{"disambiguationData":[TD([[makeQuery(id+"F4.imprint","IMPRINT",EDGE,{"disambiguationData":[TD([[subQ3,-1.0]])],"derivedFrom":subQ1}),1.0]])]});}
            var Q1;
            {var subQ0=sQuery(id+"F4.wireOp",EDGE,"E86.bottom");var subQ1=sQuery(id+"F4.wireOp",EDGE,"E79");var subQ3=makeQuery(id+"F4.imprint","INTERSECT",VERTEX,{"derivedFrom":[subQ1,subQ0]});Q1=makeQuery(id+"F4.imprint","IMPRINT",FACE,{"disambiguationData":[TD([[makeQuery(id+"F4.imprint","IMPRINT",EDGE,{"disambiguationData":[TD([[subQ3,1.0]])],"derivedFrom":subQ1}),1.0]])]});}
            var Q2;
            Q2=makeQuery(id+"F4.imprint","IMPRINT",FACE,{"disambiguationData":[TD([[makeQuery(id+"F4.imprint","IMPRINT",EDGE,{"derivedFrom":sQuery(id+"F4.wireOp",EDGE,"E86.top")}),1.0]])]});
            var Q3;
            Q3=makeQuery(id+"F4.imprint","IMPRINT",FACE,{"disambiguationData":[TD([[makeQuery(id+"F4.imprint","IMPRINT",EDGE,{"derivedFrom":sQuery(id+"F4.wireOp",EDGE,"E84.bottom")}),-1.0]])]});
            var Q4;
            Q4=makeQuery(id+"F4.imprint","IMPRINT",FACE,{"disambiguationData":[TD([[makeQuery(id+"F4.imprint","IMPRINT",EDGE,{"derivedFrom":sQuery(id+"F4.wireOp",EDGE,"E85.bottom")}),-1.0]])]});
            extrude(context, id + "F5", {"entities" : qUnion([Q0, Q1, Q2, Q3, Q4]), "operationType" : NewBodyOperationType.REMOVE, "depth" : 43.8 * mm, "offsetDistance" : 25 * mm});
        }
        {
            var Q0;
            {var subQ0=sQuery(id+"F0.wireOp",EDGE,"E1.right");var subQ1=sQuery(id+"F0.wireOp",EDGE,"E1.bottom");Q0=makeQuery(id+"F2.boolean.opBoolean","MERGE",EDGE,{"derivedFrom":[makeQuery(id+"F1.opExtrude","SWEPT_EDGE",EDGE,{"disambiguationData":[OSD([subQ1,subQ0])]}),makeQuery(id+"F2.opExtrude","SWEPT_EDGE",EDGE,{"disambiguationData":[OSD([subQ1,subQ0])]})]});}
            var Q1;
            {var subQ0=sQuery(id+"F0.wireOp",EDGE,"E1.left");var subQ1=sQuery(id+"F0.wireOp",EDGE,"E1.bottom");Q1=makeQuery(id+"F2.boolean.opBoolean","MERGE",EDGE,{"derivedFrom":[makeQuery(id+"F1.opExtrude","SWEPT_EDGE",EDGE,{"disambiguationData":[OSD([subQ1,subQ0])]}),makeQuery(id+"F2.opExtrude","SWEPT_EDGE",EDGE,{"disambiguationData":[OSD([subQ1,subQ0])]})]});}
            fillet(context, id + "F6", {"entities" : qUnion([Q0, Q1]), "radius" : 1 * mm, "tangentPropagation" : true, "allowEdgeOverflow" : false});
        }
        {
            var Q0;
            Q0=makeQuery(id+"F1.opExtrude","CAP_EDGE",EDGE,{"disambiguationData":[OSD([sQuery(id+"F0.wireOp",EDGE,"E78.left")])],"isStart":false});
            var Q1;
            Q1=makeQuery(id+"F1.opExtrude","CAP_EDGE",EDGE,{"disambiguationData":[OSD([sQuery(id+"F0.wireOp",EDGE,"E78.bottom")])],"isStart":false});
            var Q2;
            Q2=makeQuery(id+"F1.opExtrude","CAP_EDGE",EDGE,{"disambiguationData":[OSD([sQuery(id+"F0.wireOp",EDGE,"E78.top")])],"isStart":false});
            var Q3;
            Q3=makeQuery(id+"F1.opExtrude","CAP_EDGE",EDGE,{"disambiguationData":[OSD([sQuery(id+"F0.wireOp",EDGE,"E78.right")])],"isStart":false});
            chamfer(context, id + "F7", {"entities" : qUnion([Q0, Q1, Q2, Q3]), "width" : 1 * mm, "tangentPropagation" : true});
        }
    });
